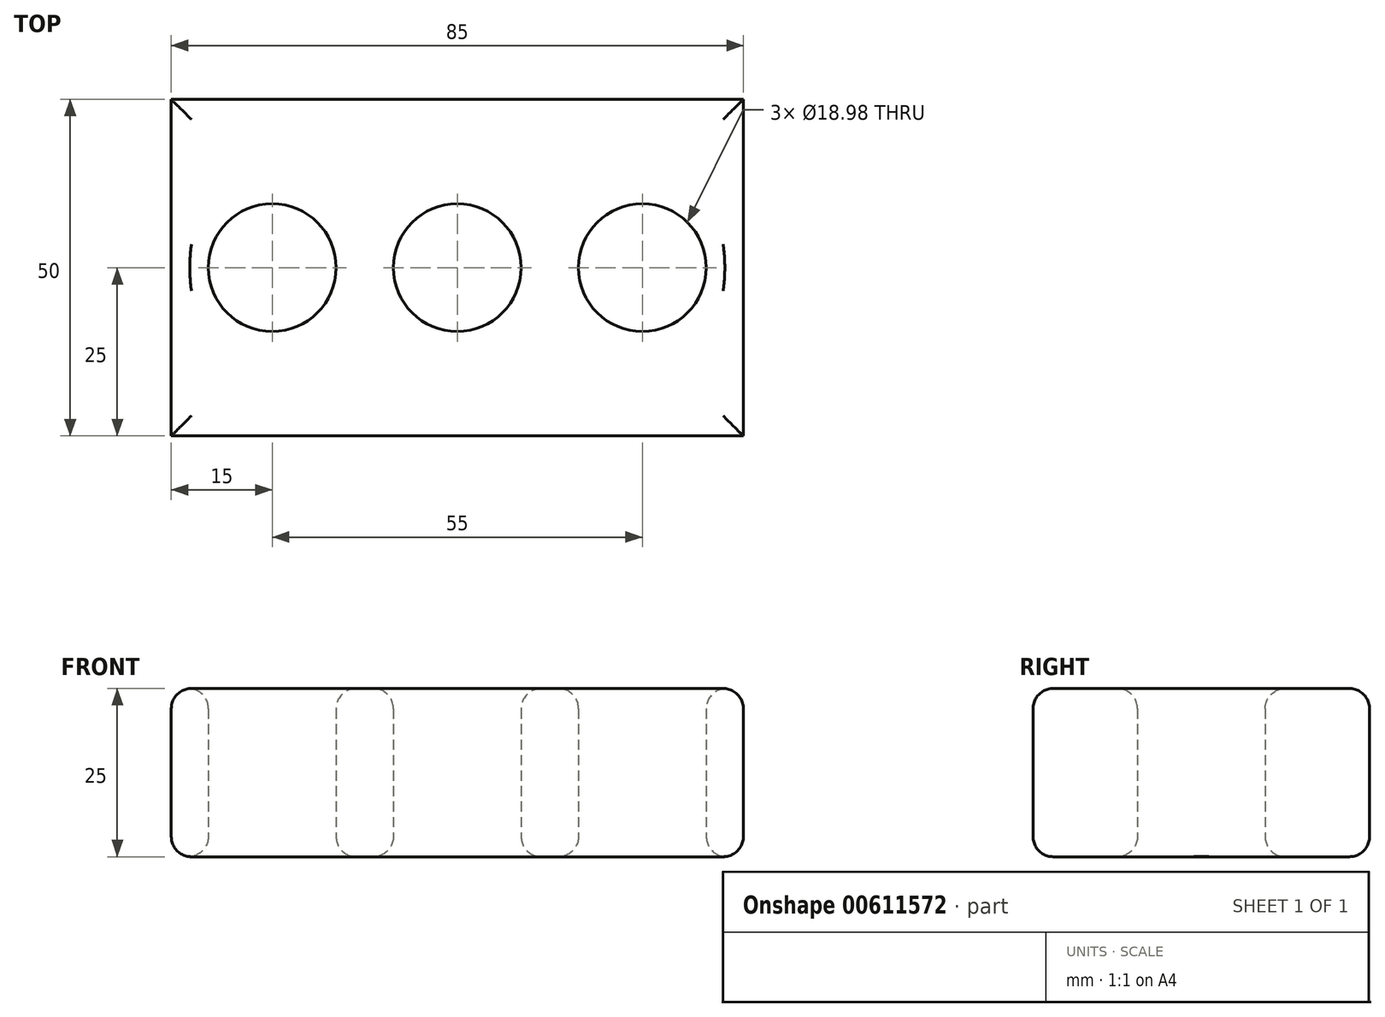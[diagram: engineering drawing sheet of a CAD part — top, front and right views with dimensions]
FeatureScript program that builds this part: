
annotation { "Feature Type Name" : "Feature", "Feature Type Description" : "" }
export const myFeature = defineFeature(function(context is Context, id is Id, definition is map)
    precondition{}
    {
        {
            var Q0;
            Q0=qCreatedBy(makeId("Top.planeOp"),FACE);
            var sketch = newSketch(context, id + "F0", { "sketchPlane" : qUnion([Q0])});
            skLineSegment(sketch, "E0.bottom", {"start": v(-42.5, 25) * mm, "end": v(42.5, 25) * mm});
            skLineSegment(sketch, "E0.top", {"start": v(-42.5, -25) * mm, "end": v(42.5, -25) * mm});
            skLineSegment(sketch, "E0.left", {"start": v(-42.5, 25) * mm, "end": v(-42.5, -25) * mm});
            skLineSegment(sketch, "E0.right", {"start": v(42.5, 25) * mm, "end": v(42.5, -25) * mm});
            skPoint(sketch, "E0.middle", {"position": v(0, 0) * mm});
            skCircle(sketch, "E1", {"center": v(0, 0) * mm, "radius": 9.49 * mm});
            skCircle(sketch, "E2", {"center": v(27.5, 0) * mm, "radius": 9.49 * mm});
            skCircle(sketch, "E3", {"center": v(-27.5, 0) * mm, "radius": 9.49 * mm});
            skSolve(sketch);
        }
        {
            var Q0;
            Q0=makeQuery(id+"F0.imprint","IMPRINT",FACE,{"disambiguationData":[TD([[makeQuery(id+"F0.imprint","IMPRINT",EDGE,{"derivedFrom":sQuery(id+"F0.wireOp",EDGE,"E0.bottom")}),-1.0]])]});
            extrude(context, id + "F1", {"entities" : qUnion([Q0]), "endBound" : BoundingType.SYMMETRIC, "depth" : 25 * mm, "offsetDistance" : 25 * mm});
        }
        {
            var Q0;
            Q0=makeQuery(id+"F1.opExtrude","CAP_EDGE",EDGE,{"disambiguationData":[OSD([sQuery(id+"F0.wireOp",EDGE,"E0.bottom")])],"isStart":true});
            var Q1;
            Q1=makeQuery(id+"F1.opExtrude","CAP_EDGE",EDGE,{"disambiguationData":[OSD([sQuery(id+"F0.wireOp",EDGE,"E0.left")])],"isStart":true});
            var Q2;
            Q2=makeQuery(id+"F1.opExtrude","CAP_EDGE",EDGE,{"disambiguationData":[OSD([sQuery(id+"F0.wireOp",EDGE,"E0.top")])],"isStart":true});
            var Q3;
            Q3=makeQuery(id+"F1.opExtrude","CAP_EDGE",EDGE,{"disambiguationData":[OSD([sQuery(id+"F0.wireOp",EDGE,"E0.right")])],"isStart":true});
            var Q4;
            Q4=makeQuery(id+"F1.opExtrude","CAP_EDGE",EDGE,{"disambiguationData":[OSD([sQuery(id+"F0.wireOp",EDGE,"E0.left")])],"isStart":false});
            var Q5;
            Q5=makeQuery(id+"F1.opExtrude","CAP_EDGE",EDGE,{"disambiguationData":[OSD([sQuery(id+"F0.wireOp",EDGE,"E0.bottom")])],"isStart":false});
            var Q6;
            Q6=makeQuery(id+"F1.opExtrude","CAP_EDGE",EDGE,{"disambiguationData":[OSD([sQuery(id+"F0.wireOp",EDGE,"E0.top")])],"isStart":false});
            var Q7;
            Q7=makeQuery(id+"F1.opExtrude","CAP_EDGE",EDGE,{"disambiguationData":[OSD([sQuery(id+"F0.wireOp",EDGE,"E0.right")])],"isStart":false});
            var Q8;
            Q8=makeQuery(id+"F1.opExtrude","CAP_EDGE",EDGE,{"disambiguationData":[OSD([sQuery(id+"F0.wireOp",EDGE,"E2")])],"isStart":true});
            var Q9;
            Q9=makeQuery(id+"F1.opExtrude","CAP_EDGE",EDGE,{"disambiguationData":[OSD([sQuery(id+"F0.wireOp",EDGE,"E1")])],"isStart":true});
            var Q10;
            Q10=makeQuery(id+"F1.opExtrude","CAP_EDGE",EDGE,{"disambiguationData":[OSD([sQuery(id+"F0.wireOp",EDGE,"E3")])],"isStart":true});
            var Q11;
            Q11=makeQuery(id+"F1.opExtrude","CAP_EDGE",EDGE,{"disambiguationData":[OSD([sQuery(id+"F0.wireOp",EDGE,"E2")])],"isStart":false});
            var Q12;
            Q12=makeQuery(id+"F1.opExtrude","CAP_EDGE",EDGE,{"disambiguationData":[OSD([sQuery(id+"F0.wireOp",EDGE,"E1")])],"isStart":false});
            var Q13;
            Q13=makeQuery(id+"F1.opExtrude","CAP_EDGE",EDGE,{"disambiguationData":[OSD([sQuery(id+"F0.wireOp",EDGE,"E3")])],"isStart":false});
            fillet(context, id + "F2", {"entities" : qUnion([Q0, Q1, Q2, Q3, Q4, Q5, Q6, Q7, Q8, Q9, Q10, Q11, Q12, Q13]), "radius" : 3 * mm, "tangentPropagation" : true, "allowEdgeOverflow" : false});
        }
    });
